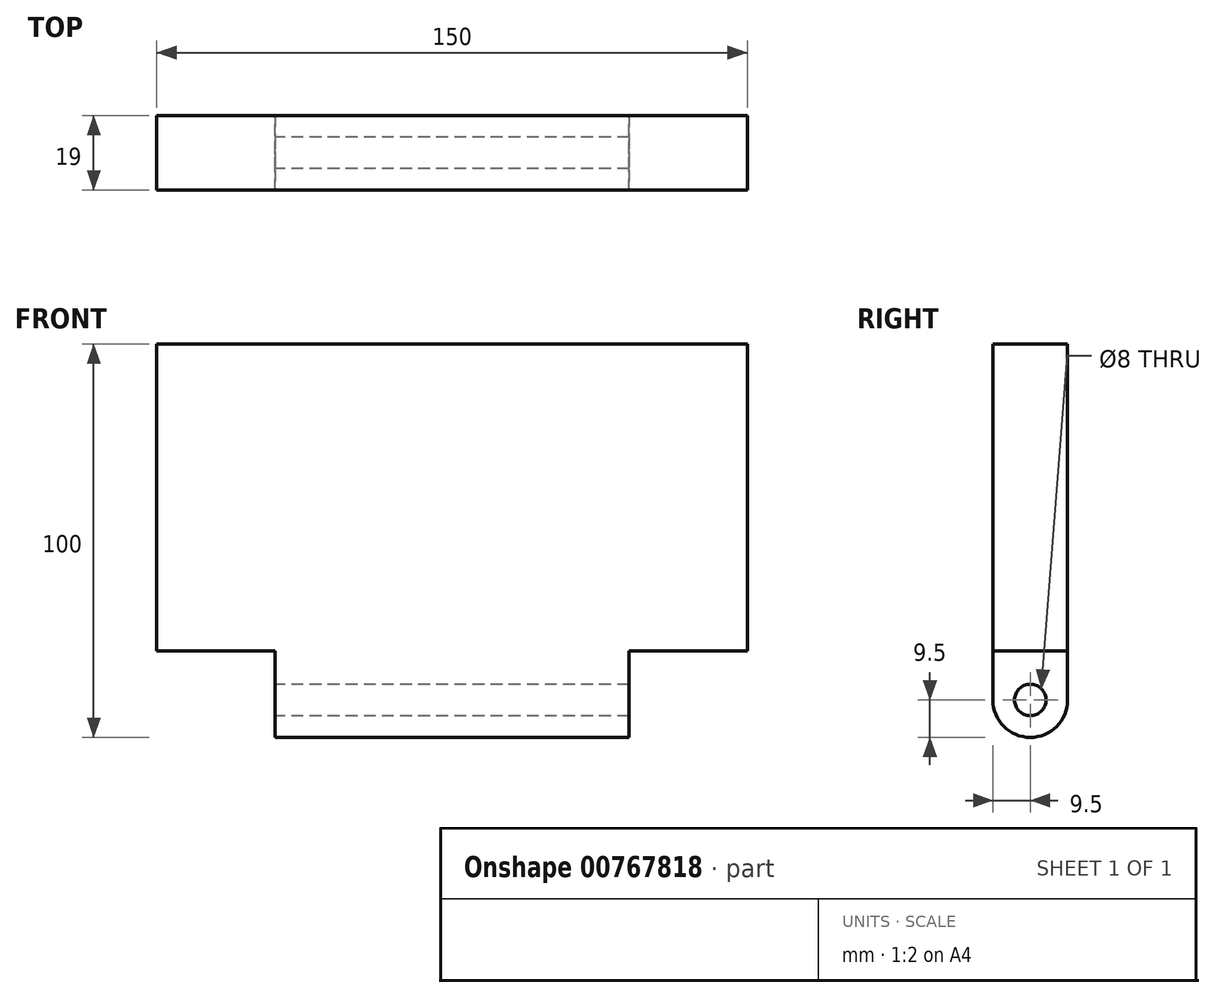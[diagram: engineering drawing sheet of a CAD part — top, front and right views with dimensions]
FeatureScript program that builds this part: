
annotation { "Feature Type Name" : "Feature", "Feature Type Description" : "" }
export const myFeature = defineFeature(function(context is Context, id is Id, definition is map)
    precondition{}
    {
        {
            var Q0;
            Q0=qCreatedBy(makeId("Front.planeOp"),FACE);
            var sketch = newSketch(context, id + "F0", { "sketchPlane" : qUnion([Q0])});
            skLineSegment(sketch, "E0.bottom", {"start": v(45, -50) * mm, "end": v(-45, -50) * mm});
            skLineSegment(sketch, "E0.top", {"start": v(75, 50) * mm, "end": v(-75, 50) * mm});
            skLineSegment(sketch, "E0.left", {"start": v(75, -28) * mm, "end": v(75, 50) * mm});
            skLineSegment(sketch, "E0.right", {"start": v(-75, -28) * mm, "end": v(-75, 50) * mm});
            skPoint(sketch, "E0.middle", {"position": v(0, 0) * mm});
            skLineSegment(sketch, "E1.top", {"start": v(-75, -28) * mm, "end": v(-45, -28) * mm});
            skLineSegment(sketch, "E1.right", {"start": v(-45, -50) * mm, "end": v(-45, -28) * mm});
            skLineSegment(sketch, "E2.top", {"start": v(75, -28) * mm, "end": v(45, -28) * mm});
            skLineSegment(sketch, "E2.right", {"start": v(45, -50) * mm, "end": v(45, -28) * mm});
            skPoint(sketch, "E3.orphan", {"position": v(-75, -50) * mm});
            skPoint(sketch, "E4.orphan", {"position": v(75, -50) * mm});
            skSolve(sketch);
        }
        {
            var Q0;
            Q0=makeQuery(id+"F0.imprint","IMPRINT",FACE,{"disambiguationData":[TD([[makeQuery(id+"F0.imprint","IMPRINT",EDGE,{"derivedFrom":sQuery(id+"F0.wireOp",EDGE,"E0.bottom")}),-1.0]])]});
            extrude(context, id + "F1", {"entities" : qUnion([Q0]), "depth" : 19 * mm, "offsetDistance" : 25 * mm});
        }
        {
            var Q0;
            Q0=makeQuery(id+"F1.opExtrude","SWEPT_FACE",FACE,{"disambiguationData":[OSD([sQuery(id+"F0.wireOp",EDGE,"E1.right")])]});
            var sketch = newSketch(context, id + "F2", { "sketchPlane" : qUnion([Q0])});
            skLineSegment(sketch, "E5", {"start": v(0, -31) * mm, "end": v(19, -31) * mm, "construction": true});
            skLineSegment(sketch, "E6", {"start": v(0, -31) * mm, "end": v(19, -50) * mm, "construction": true});
            skCircle(sketch, "E7", {"center": v(9.5, -40.5) * mm, "radius": 4 * mm});
            skSolve(sketch);
        }
        {
            var Q0;
            Q0=makeQuery(id+"F2.imprint","IMPRINT",FACE,{"disambiguationData":[TD([[makeQuery(id+"F2.imprint","IMPRINT",EDGE,{"derivedFrom":sQuery(id+"F2.wireOp",EDGE,"E7")}),1.0]])]});
            extrude(context, id + "F3", {"entities" : qUnion([Q0]), "operationType" : NewBodyOperationType.REMOVE, "endBound" : BoundingType.THROUGH_ALL, "oppositeDirection" : true, "depth" : 25 * mm, "offsetDistance" : 25 * mm});
        }
        {
            var Q0;
            Q0=makeQuery(id+"F1.opExtrude","CAP_EDGE",EDGE,{"disambiguationData":[OSD([sQuery(id+"F0.wireOp",EDGE,"E0.bottom")])],"isStart":true});
            var Q1;
            Q1=makeQuery(id+"F1.opExtrude","CAP_EDGE",EDGE,{"disambiguationData":[OSD([sQuery(id+"F0.wireOp",EDGE,"E0.bottom")])],"isStart":false});
            fillet(context, id + "F4", {"entities" : qUnion([Q0, Q1]), "radius" : 9.5 * mm, "tangentPropagation" : true, "allowEdgeOverflow" : false});
        }
    });
